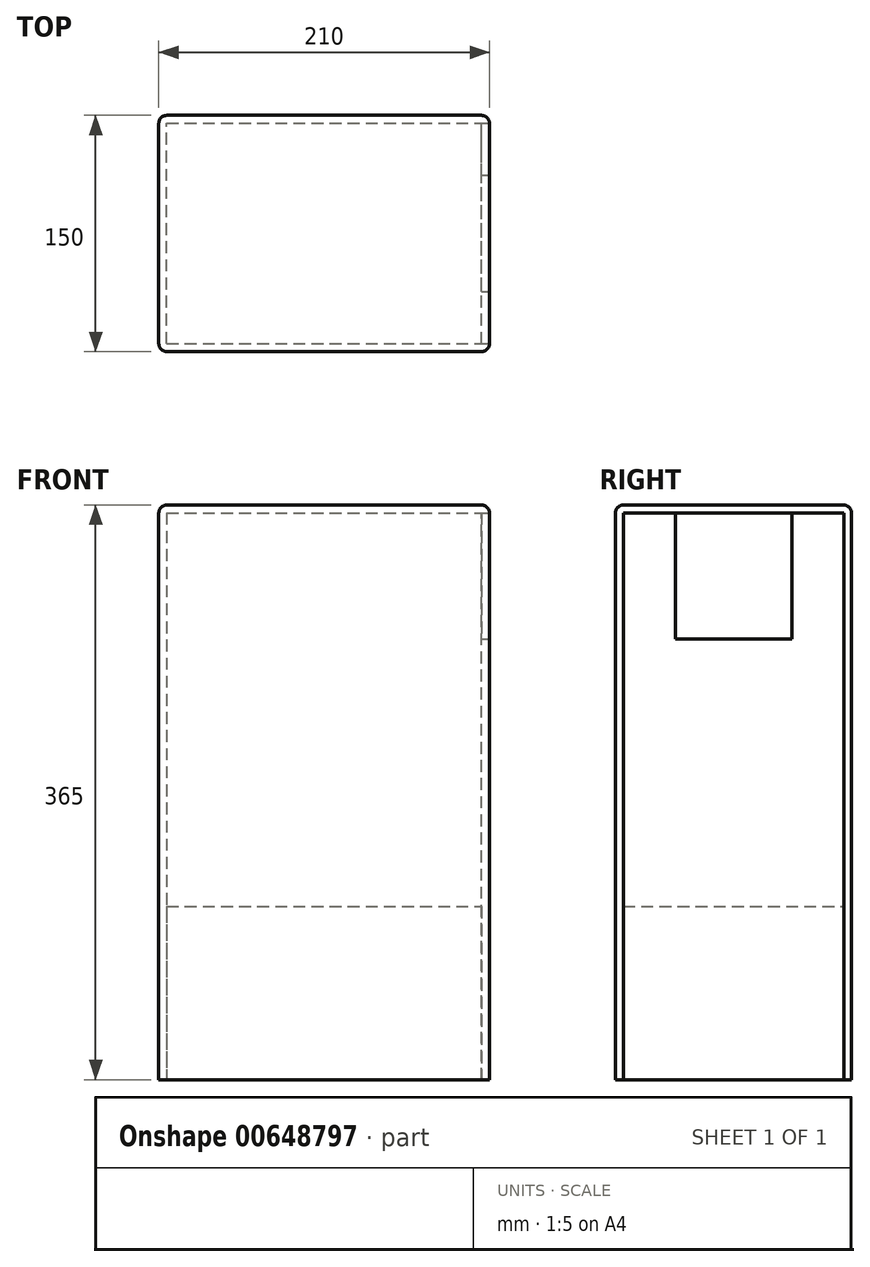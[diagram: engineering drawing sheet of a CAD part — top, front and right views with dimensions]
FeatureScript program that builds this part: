
annotation { "Feature Type Name" : "Feature", "Feature Type Description" : "" }
export const myFeature = defineFeature(function(context is Context, id is Id, definition is map)
    precondition{}
    {
        {
            var Q0;
            Q0=qCreatedBy(makeId("Front.planeOp"),FACE);
            var sketch = newSketch(context, id + "F0", { "sketchPlane" : qUnion([Q0])});
            skLineSegment(sketch, "E0.bottom", {"start": v(0, 0) * mm, "end": v(205, 0) * mm});
            skLineSegment(sketch, "E0.top", {"start": v(0, 360) * mm, "end": v(205, 360) * mm});
            skLineSegment(sketch, "E0.left", {"start": v(0, 0) * mm, "end": v(0, 360) * mm});
            skLineSegment(sketch, "E0.right", {"start": v(205, 0) * mm, "end": v(205, 360) * mm});
            skSolve(sketch);
        }
        {
            var Q0;
            Q0=makeQuery(id+"F0.imprint","IMPRINT",FACE,{"disambiguationData":[TD([[makeQuery(id+"F0.imprint","IMPRINT",EDGE,{"derivedFrom":sQuery(id+"F0.wireOp",EDGE,"E0.bottom")}),1.0]])]});
            extrude(context, id + "F1", {"entities" : qUnion([Q0]), "depth" : 5 * mm, "offsetDistance" : 25 * mm});
        }
        {
            var Q0;
            Q0=makeQuery(id+"F1.opExtrude","SWEPT_FACE",FACE,{"disambiguationData":[OSD([sQuery(id+"F0.wireOp",EDGE,"E0.left")])]});
            var sketch = newSketch(context, id + "F2", { "sketchPlane" : qUnion([Q0])});
            skLineSegment(sketch, "E1.bottom", {"start": v(5, 360) * mm, "end": v(-145, 360) * mm});
            skLineSegment(sketch, "E1.top", {"start": v(5, 0) * mm, "end": v(-145, 0) * mm});
            skLineSegment(sketch, "E1.left", {"start": v(5, 360) * mm, "end": v(5, 0) * mm});
            skLineSegment(sketch, "E1.right", {"start": v(-145, 360) * mm, "end": v(-145, 0) * mm});
            skSolve(sketch);
        }
        {
            var Q0;
            Q0 = qSketchRegion(id + "F2", true);
            extrude(context, id + "F3", {"entities" : qUnion([Q0]), "operationType" : NewBodyOperationType.ADD, "depth" : 5 * mm, "offsetDistance" : 25 * mm});
        }
        {
            var Q0;
            Q0=makeQuery(id+"F3.opExtrude","SWEPT_FACE",FACE,{"disambiguationData":[OSD([sQuery(id+"F2.wireOp",EDGE,"E1.right")])]});
            var sketch = newSketch(context, id + "F4", { "sketchPlane" : qUnion([Q0])});
            skLineSegment(sketch, "E2.bottom", {"start": v(0, 360) * mm, "end": v(-205, 360) * mm});
            skLineSegment(sketch, "E2.top", {"start": v(0, 0) * mm, "end": v(-205, 0) * mm});
            skLineSegment(sketch, "E2.left", {"start": v(0, 360) * mm, "end": v(0, 0) * mm});
            skLineSegment(sketch, "E2.right", {"start": v(-205, 360) * mm, "end": v(-205, 0) * mm});
            skSolve(sketch);
        }
        {
            var Q0;
            Q0=makeQuery(id+"F4.imprint","IMPRINT",FACE,{"disambiguationData":[TD([[makeQuery(id+"F4.imprint","IMPRINT",EDGE,{"derivedFrom":sQuery(id+"F4.wireOp",EDGE,"E2.bottom")}),1.0]])]});
            extrude(context, id + "F5", {"entities" : qUnion([Q0]), "operationType" : NewBodyOperationType.ADD, "oppositeDirection" : true, "depth" : 5 * mm, "offsetDistance" : 25 * mm});
        }
        {
            var Q0;
            Q0=makeQuery(id+"F5.boolean.opBoolean","MERGE",FACE,{"derivedFrom":[makeQuery(id+"F3.boolean.opBoolean","MERGE",FACE,{"derivedFrom":[makeQuery(id+"F1.opExtrude","SWEPT_FACE",FACE,{"disambiguationData":[OSD([sQuery(id+"F0.wireOp",EDGE,"E0.top")])]}),makeQuery(id+"F3.opExtrude","SWEPT_FACE",FACE,{"disambiguationData":[OSD([sQuery(id+"F2.wireOp",EDGE,"E1.bottom")])]})]}),makeQuery(id+"F5.opExtrude","SWEPT_FACE",FACE,{"disambiguationData":[OSD([sQuery(id+"F4.wireOp",EDGE,"E2.bottom")])]})]});
            var sketch = newSketch(context, id + "F6", { "sketchPlane" : qUnion([Q0])});
            skLineSegment(sketch, "E3.bottom", {"start": v(-5, -5) * mm, "end": v(205, -5) * mm});
            skLineSegment(sketch, "E3.top", {"start": v(-5, 145) * mm, "end": v(205, 145) * mm});
            skLineSegment(sketch, "E3.left", {"start": v(-5, -5) * mm, "end": v(-5, 145) * mm});
            skLineSegment(sketch, "E3.right", {"start": v(205, -5) * mm, "end": v(205, 145) * mm});
            skSolve(sketch);
        }
        {
            var Q0;
            {var subQ3=sQuery(id+"F6.wireOp",EDGE,"E3.bottom");Q0=makeQuery(id+"F6.imprint","IMPRINT",FACE,{"disambiguationData":[TD([[makeQuery(id+"F6.imprint","IMPRINT",EDGE,{"derivedFrom":subQ3}),1.0]])]});}
            var Q1;
            {var subQ1=makeQuery(id+"F1.opExtrude","CAP_EDGE",EDGE,{"disambiguationData":[OSD([sQuery(id+"F0.wireOp",EDGE,"E0.top")])],"isStart":true});Q1=makeQuery(id+"F6.imprint","IMPRINT",FACE,{"disambiguationData":[TD([[makeQuery(id+"F6.imprint","IMPRINT",EDGE,{"derivedFrom":subQ1}),1.0]])]});}
            extrude(context, id + "F7", {"entities" : qUnion([Q0, Q1]), "operationType" : NewBodyOperationType.ADD, "depth" : 5 * mm, "offsetDistance" : 25 * mm});
        }
        {
            var Q0;
            Q0=makeQuery(id+"F7.boolean.opBoolean","MERGE",FACE,{"derivedFrom":[makeQuery(id+"F1.opExtrude","SWEPT_FACE",FACE,{"disambiguationData":[OSD([sQuery(id+"F0.wireOp",EDGE,"E0.right")])]}),makeQuery(id+"F5.opExtrude","SWEPT_FACE",FACE,{"disambiguationData":[OSD([sQuery(id+"F4.wireOp",EDGE,"E2.right")])]}),makeQuery(id+"F7.opExtrude","SWEPT_FACE",FACE,{"disambiguationData":[OSD([sQuery(id+"F6.wireOp",EDGE,"E3.right")])]})]});
            var sketch = newSketch(context, id + "F8", { "sketchPlane" : qUnion([Q0])});
            skLineSegment(sketch, "E4.bottom", {"start": v(-5, 365) * mm, "end": v(145, 365) * mm});
            skLineSegment(sketch, "E4.top", {"start": v(-5, 0) * mm, "end": v(145, 0) * mm});
            skLineSegment(sketch, "E4.left", {"start": v(-5, 365) * mm, "end": v(-5, 0) * mm});
            skLineSegment(sketch, "E4.right", {"start": v(145, 365) * mm, "end": v(145, 0) * mm});
            skLineSegment(sketch, "E5", {"start": v(-5, 365) * mm, "end": v(33, 365) * mm});
            skLineSegment(sketch, "E6", {"start": v(145, 365) * mm, "end": v(107, 365) * mm});
            skLineSegment(sketch, "E7", {"start": v(33, 365) * mm, "end": v(33, 280) * mm});
            skLineSegment(sketch, "E8", {"start": v(33, 280) * mm, "end": v(107, 280) * mm});
            skLineSegment(sketch, "E9", {"start": v(107, 365) * mm, "end": v(107, 280) * mm});
            skSolve(sketch);
        }
        {
            var Q0;
            {var subQ1=sQuery(id+"F8.wireOp",EDGE,"E8");Q0=makeQuery(id+"F8.imprint","IMPRINT",FACE,{"disambiguationData":[TD([[makeQuery(id+"F8.imprint","IMPRINT",EDGE,{"derivedFrom":subQ1}),-1.0]])]});}
            extrude(context, id + "F9", {"entities" : qUnion([Q0]), "oppositeDirection" : true, "depth" : 5 * mm, "offsetDistance" : 25 * mm});
        }
        {
            var Q0;
            Q0=makeQuery(id+"F7.boolean.opBoolean","MERGE",EDGE,{"derivedFrom":[makeQuery(id+"F1.opExtrude","CAP_EDGE",EDGE,{"disambiguationData":[OSD([sQuery(id+"F0.wireOp",EDGE,"E0.right")])],"isStart":false}),makeQuery(id+"F7.opExtrude","SWEPT_EDGE",EDGE,{"disambiguationData":[OSD([sQuery(id+"F6.wireOp",EDGE,"E3.bottom"),sQuery(id+"F6.wireOp",EDGE,"E3.right")])]})]});
            fillet(context, id + "F10", {"entities" : qUnion([Q0]), "radius" : 5 * mm, "tangentPropagation" : true, "allowEdgeOverflow" : false});
        }
        {
            var Q0;
            Q0=makeQuery(id+"F7.opExtrude","CAP_EDGE",EDGE,{"disambiguationData":[OSD([sQuery(id+"F6.wireOp",EDGE,"E3.right")])],"isStart":false});
            fillet(context, id + "F11", {"entities" : qUnion([Q0]), "radius" : 5 * mm, "tangentPropagation" : true, "allowEdgeOverflow" : false});
        }
        {
            var Q0;
            Q0=makeQuery(id+"F7.boolean.opBoolean","MERGE",EDGE,{"derivedFrom":[makeQuery(id+"F5.opExtrude","CAP_EDGE",EDGE,{"disambiguationData":[OSD([sQuery(id+"F4.wireOp",EDGE,"E2.right")])],"isStart":true}),makeQuery(id+"F7.opExtrude","SWEPT_EDGE",EDGE,{"disambiguationData":[OSD([sQuery(id+"F6.wireOp",EDGE,"E3.top"),sQuery(id+"F6.wireOp",EDGE,"E3.right")])]})]});
            fillet(context, id + "F12", {"entities" : qUnion([Q0]), "radius" : 5 * mm, "tangentPropagation" : true, "allowEdgeOverflow" : false});
        }
        {
            var Q0;
            Q0=makeQuery(id+"F7.opExtrude","CAP_EDGE",EDGE,{"disambiguationData":[OSD([sQuery(id+"F6.wireOp",EDGE,"E3.left")])],"isStart":false});
            fillet(context, id + "F13", {"entities" : qUnion([Q0]), "radius" : 5 * mm, "tangentPropagation" : true, "allowEdgeOverflow" : false});
        }
        {
            var Q0;
            Q0=qCreatedBy(makeId("Top.planeOp"),FACE);
            var sketch = newSketch(context, id + "F14", { "sketchPlane" : qUnion([Q0])});
            skLineSegment(sketch, "E10.bottom", {"start": v(0, 0) * mm, "end": v(200, 0) * mm});
            skLineSegment(sketch, "E10.top", {"start": v(0, 140) * mm, "end": v(200, 140) * mm});
            skLineSegment(sketch, "E10.left", {"start": v(0, 0) * mm, "end": v(0, 140) * mm});
            skLineSegment(sketch, "E10.right", {"start": v(200, 0) * mm, "end": v(200, 140) * mm});
            skSolve(sketch);
        }
        {
            var Q0;
            Q0=makeQuery(id+"F14.imprint","IMPRINT",FACE,{"disambiguationData":[TD([[makeQuery(id+"F14.imprint","IMPRINT",EDGE,{"derivedFrom":sQuery(id+"F14.wireOp",EDGE,"E10.bottom")}),1.0]])]});
            extrude(context, id + "F15", {"entities" : qUnion([Q0]), "depth" : 110 * mm, "offsetDistance" : 25 * mm});
        }
    });
